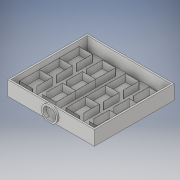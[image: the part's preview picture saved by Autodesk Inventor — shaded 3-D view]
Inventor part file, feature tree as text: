
AUTODESK INVENTOR PART (.ipt)
format: ipt  version: 2017 (Build 210142000, 142)  size: 342,528 bytes
history: native  units: in
note: dims shown in document units (in); Inventor stores cm internally (conversion verified against a paired STEP export)
features: extrude x6, sketch x5
ambient origin geometry x8: Origin, YZ Plane, XZ Plane, XY Plane, X Axis, Y Axis, Z Axis, Center Point
bodies: Solid1 (feature_tree), Solid2 (feature_tree)
feature tree (11):
  extrude  "cubicals"  Depth=12.0in
  extrude  "floor"  Depth=2.5in
  extrude  "walls"  Depth=0.0833in
  sketch  "Sketch4"  dims[d10=0.0833in d95=0.0833in]
  extrude  "connection"  Depth=0.0833in
  extrude  "light connection"  Depth=2.5in
  extrude  "connection cut"  Depth=2.5in
  sketch  "Sketch2"  dims[d2=4.5in d3=0.0in d4=12.0in]
  sketch  "Sketch3"  dims[d5=8.0in d7=2.5in]
  sketch  "Sketch5"  dims[d97=0.0833in d98=0.0833in]
  sketch  "Sketch6"  dims[d99=12.0in d100=8.0in d102=0.0833in d103=0.0833in d104=0.0833in d105=0.0833in d106=12.0in d107=8.0in d109=0.0833in d110=0.0833in d111=0.0833in d112=0.0833in d113=2.5in d114=2.5in d115=3.0in d117=3.0in d118=6.0in d120=6.0in d121=1.0in d122=0.0in d128=1.0in d129=1.0in d130=1.0in d131=1.0in d132=1.0in d133=1.0in d134=7.7746in d135=0.0in d148=4.0in d149=1.0in d150=4.8944in d151=0.5833in d152=3.8873in d153=3.8873in d154=1.7083in d155=0.0625in d156=0.0625in d157=1.6458in d158=0.125in d159=0.125in d160=1.0in d161=0.0in d164=0.25in d165=0.125in d166=45.0deg d167=0.0892in d168=0.0884in d169=1.0in d170=0.0in d171=1.0in d172=0.0in]
